FCSTD DOCUMENT  (FreeCAD 1.0R38806 (Git))
Label: Upper Body Asembly
License: All rights reserved
LicenseURL: http://en.wikipedia.org/wiki/All_rights_reserved
objects: App::FeaturePython×4, App::Link×3, Assembly::JointGroup×1, Assembly::AssemblyObject×1
EXTERNAL_REF file=Screen Fitting.FCStd obj=Body
EXTERNAL_REF file=Front Panel.FCStd obj=Body
EXTERNAL_REF file=Walls.FCStd obj=Body

FEATURE [App::Link] Body
  LinkPlacement = pos=(2,53,-1) rot=(0,0,1;0rad)
  LinkedObject = -> <external Screen Fitting.FCStd>#Body
  Placement = pos=(2,53,-1) rot=(0,0,1;0rad)
FEATURE [App::Link] Body001
  LinkPlacement = pos=(-7.99998,8.00001,-1.8e-15) rot=(0,0,1;0rad)
  LinkedObject = -> <external Front Panel.FCStd>#Body
  Placement = pos=(-7.99998,8.00001,-1.8e-15) rot=(0,0,1;0rad)
FEATURE [App::Link] Body002
  LinkPlacement = pos=(-8.00001,8.00002,-60) rot=(0,0,1;0rad)
  LinkedObject = -> <external Walls.FCStd>#Body
  Placement = pos=(-8.00001,8.00002,-60) rot=(0,0,1;0rad)
FEATURE [App::FeaturePython] Fixed  # Assembly joint (typed FeaturePython)
  Activated = true
  AngleMax = 0
  AngleMin = 0
  Detach1 = false
  Detach2 = false
  Distance = 0
  Distance2 = 0
  EnableAngleMax = false
  EnableAngleMin = false
  EnableLengthMax = false
  EnableLengthMin = false
  JointType = 0 (Fixed)
  LengthMax = 0
  LengthMin = 0
  Placement1 = pos=(10,110,0) rot=(0,0,1;0rad)
  Placement2 = pos=(2,118,60) rot=(0,0,1;0rad)
  Reference1 = -> Assembly [Body001.Fillet.Face2,Body001.Fillet.Vertex36]
  Reference2 = -> Assembly [Body002.Fillet.Face5,Body002.Fillet.Vertex21]
FEATURE [App::FeaturePython] GroundedJoint  # Assembly grounded joint (typed FeaturePython)
  ObjectToGround = -> Body001
  Placement = pos=(-7.99998,8.00001,-1.8e-15) rot=(0,0,1;0rad)
FEATURE [App::FeaturePython] GroundedJoint001  # Assembly grounded joint (typed FeaturePython)
  ObjectToGround = -> Body
  Placement = pos=(2,53,-1) rot=(0,0,1;0rad)
FEATURE [App::FeaturePython] GroundedJoint002  # Assembly grounded joint (typed FeaturePython)
  ObjectToGround = -> Body002
  Placement = pos=(-8.00001,8.00002,-60) rot=(0,0,1;0rad)
FEATURE [Assembly::JointGroup] Joints
  Group = -> [Fixed,GroundedJoint,GroundedJoint001,GroundedJoint002]
FEATURE [Assembly::AssemblyObject] Assembly
  Group = -> [Joints,Body,Body001,Body002,Fixed,GroundedJoint,GroundedJoint001,GroundedJoint002]
  Origin = -> Origin
  Type = Assembly

RESOLVED EXTERNAL PARTS (link-assembly join: the EXTERNAL_REF files above that resolve inside this repo's crawl, each included once):
---- part Walls.FCStd = doc fcstd_c6c1d585da91 ----
FCSTD DOCUMENT  (FreeCAD 1.0R38806 (Git))
Label: Walls
License: All rights reserved
LicenseURL: https://en.wikipedia.org/wiki/All_rights_reserved
objects: Sketcher::SketchObject×5, PartDesign::Plane×2, PartDesign::Pocket×2, PartDesign::Pad×1, PartDesign::Fillet×1, PartDesign::Body×1
note: 25 computed .brp shape members not serialized (recipe doc carries the construction recipe); baked Part::Feature solids carry a one-line shape summary decoded from their .brp

FEATURE [Sketcher::SketchObject] Sketch  label="Base"
  ArcFitTolerance = 0
  FullyConstrained = true
  MakeInternals = false
  MapMode = 5
  sketch-geometry (4):
    g0: LineSegment StartX=0 StartY=0 StartZ=0 EndX=150 EndY=0 EndZ=0
    g1: LineSegment StartX=150 StartY=0 StartZ=0 EndX=150 EndY=120 EndZ=0
    g2: LineSegment StartX=150 StartY=120 StartZ=0 EndX=0 EndY=120 EndZ=0
    g3: LineSegment StartX=0 StartY=120 StartZ=0 EndX=0 EndY=0 EndZ=0
  constraints (11):
    c: Coincident(g0,g1)
    c: Coincident(g1,g2)
    c: Coincident(g2,g3)
    c: Coincident(g3,g0)
    c: Horizontal(g0)
    c: Horizontal(g2)
    c: Vertical(g1)
    c: Vertical(g3)
    c: Coincident(g0,g-1)
    c: DistanceY(g3,g3) = 120  'height'
    c: DistanceX(g2,g2) = 150  'width'
FEATURE [Sketcher::SketchObject] Sketch001  label="Left"
  ArcFitTolerance = 0
  ExternalGeometry = -> [Sketch]
  FullyConstrained = true
  MakeInternals = false
  MapMode = 5
  Placement = pos=(0,0,0) rot=(0.57735,0.57735,0.57735;2.0944rad)
  sketch-geometry (4):
    g0: LineSegment StartX=0 StartY=0 StartZ=0 EndX=120 EndY=0 EndZ=0
    g1: LineSegment StartX=120 StartY=0 StartZ=0 EndX=120 EndY=60 EndZ=0
    g2: LineSegment StartX=120 StartY=60 StartZ=0 EndX=0 EndY=60 EndZ=0
    g3: LineSegment StartX=0 StartY=60 StartZ=0 EndX=0 EndY=0 EndZ=0
  constraints (10):
    c: Coincident(g0,g1)
    c: Coincident(g1,g2)
    c: Coincident(g2,g3)
    c: Coincident(g3,g0)
    c: Horizontal(g2)
    c: Vertical(g1)
    c: Vertical(g3)
    c: Coincident(g0,g-1)
    c: Coincident(g0,g-3)
    c: DistanceY(g3,g3) = 60  'gameboy_depth'
FEATURE [Sketcher::SketchObject] Sketch002  label="Front"
  ArcFitTolerance = 0
  ExternalGeometry = -> [Sketch001,Sketch]
  FullyConstrained = true
  MakeInternals = false
  MapMode = 5
  Placement = pos=(0,0,0) rot=(1,0,0;1.5708rad)
  sketch-geometry (4):
    g0: LineSegment StartX=0 StartY=60 StartZ=0 EndX=0 EndY=0 EndZ=0
    g1: LineSegment StartX=0 StartY=0 StartZ=0 EndX=150 EndY=0 EndZ=0
    g2: LineSegment StartX=150 StartY=0 StartZ=0 EndX=150 EndY=60 EndZ=0
    g3: LineSegment StartX=150 StartY=60 StartZ=0 EndX=0 EndY=60 EndZ=0
  constraints (10):
    c: Coincident(g0,g1)
    c: Coincident(g1,g2)
    c: Coincident(g2,g3)
    c: Coincident(g3,g0)
    c: Vertical(g0)
    c: Vertical(g2)
    c: Horizontal(g1)
    c: Horizontal(g3)
    c: Coincident(g0,g-3)
    c: Coincident(g1,g-4)
FEATURE [PartDesign::Plane] DatumPlane
  AttachmentOffset = pos=(0,0,-120) rot=(0,0,1;0rad)
  Length = 199.393
  MapMode = 5
  Placement = pos=(0,120,-2.4e-14) rot=(1,0,0;1.5708rad)
  ResizeMode = 0
  Width = 109.393
  expr: .AttachmentOffset.Base.z = -1 * <<Base>>.Constraints.height
FEATURE [PartDesign::Plane] DatumPlane001
  AttachmentOffset = pos=(0,0,150) rot=(0,0,1;0rad)
  Length = 167.204
  MapMode = 5
  Placement = pos=(125,0,0) rot=(0.57735,0.57735,0.57735;2.0944rad)
  ResizeMode = 0
  Width = 107.204
  expr: .AttachmentOffset.Base.z = <<Base>>.Constraints.width
FEATURE [Sketcher::SketchObject] Sketch003  label="Cutout"
  ArcFitTolerance = 0
  ExternalGeometry = -> [Sketch]
  FullyConstrained = true
  MakeInternals = false
  MapMode = 5
  expr: Constraints[10] = .Constraints.border_x
  expr: Constraints[11] = .Constraints.border_y
  sketch-geometry (4):
    g0: LineSegment StartX=2 StartY=118 StartZ=0 EndX=2 EndY=2 EndZ=0
    g1: LineSegment StartX=2 StartY=2 StartZ=0 EndX=148 EndY=2 EndZ=0
    g2: LineSegment StartX=148 StartY=2 StartZ=0 EndX=148 EndY=118 EndZ=0
    g3: LineSegment StartX=148 StartY=118 StartZ=0 EndX=2 EndY=118 EndZ=0
  constraints (12):
    c: Coincident(g0,g1)
    c: Coincident(g1,g2)
    c: Coincident(g2,g3)
    c: Coincident(g3,g0)
    c: Vertical(g0)
    c: Vertical(g2)
    c: Horizontal(g1)
    c: Horizontal(g3)
    c: DistanceX(g-1,g0) = 2  'border_x'
    c: Distance(g0,g-1) = 2  'border_y'
    c: DistanceX(g2,g-3) = 2
    c: DistanceY(g2,g-3) = 2
FEATURE [PartDesign::Pad] Pad
  Direction = (0,0,1)
  Length = 60
  Length2 = 10
  Profile = -> Sketch
  ReferenceAxis = -> Sketch [N_Axis]
  Refine = true
  Suppressed = false
  Type = 0
  expr: Length = <<Left>>.Constraints.gameboy_depth
FEATURE [PartDesign::Pocket] Pocket
  BaseFeature = -> Pad
  Direction = (0,0,-1)
  Length = 60
  Length2 = 5
  Profile = -> Sketch003
  ReferenceAxis = -> Sketch003 [N_Axis]
  Refine = true
  Reversed = true
  Suppressed = false
  Type = 0
  expr: Length = <<Left>>.Constraints.gameboy_depth
FEATURE [Sketcher::SketchObject] Sketch004  label="BackSwitchHole"
  ArcFitTolerance = 0
  FullyConstrained = true
  MakeInternals = false
  MapMode = 5
  Placement = pos=(0,120,-2.4e-14) rot=(1,0,0;1.5708rad)
  sketch-geometry (1):
    g0: Circle CenterX=125 CenterY=30 CenterZ=0 NormalX=0 NormalY=0 NormalZ=1 AngleXU=0 Radius=6.5
  constraints (3):
    c: Diameter(g0) = 13  'power_switch_hole_diameter'
    c: DistanceY(g-1,g0) = 30  'power_switch_y'
    c: DistanceX(g-1,g0) = 125  'power_switch_x'
FEATURE [PartDesign::Pocket] Pocket001
  BaseFeature = -> Pocket
  Direction = (0,1,0)
  Length = 2
  Length2 = 5
  Profile = -> Sketch004
  ReferenceAxis = -> Sketch004 [N_Axis]
  Refine = true
  Reversed = true
  Suppressed = false
  Type = 0
  expr: Length = <<Cutout>>.Constraints.border_y
FEATURE [PartDesign::Fillet] Fillet
  Base = -> Pocket001 [Edge2,Edge1,Edge5,Edge8]
  BaseFeature = -> Pocket001
  Radius = 1.9
  Refine = true
  SupportTransform = false
  Suppressed = false
  UseAllEdges = false
FEATURE [PartDesign::Body] Body
  AllowCompound = false
  Group = -> [Sketch,Sketch001,Sketch002,DatumPlane,DatumPlane001,Sketch003,Pad,Pocket,Sketch004,Pocket001,Fillet]
  Origin = -> Origin
  Tip = -> Fillet
